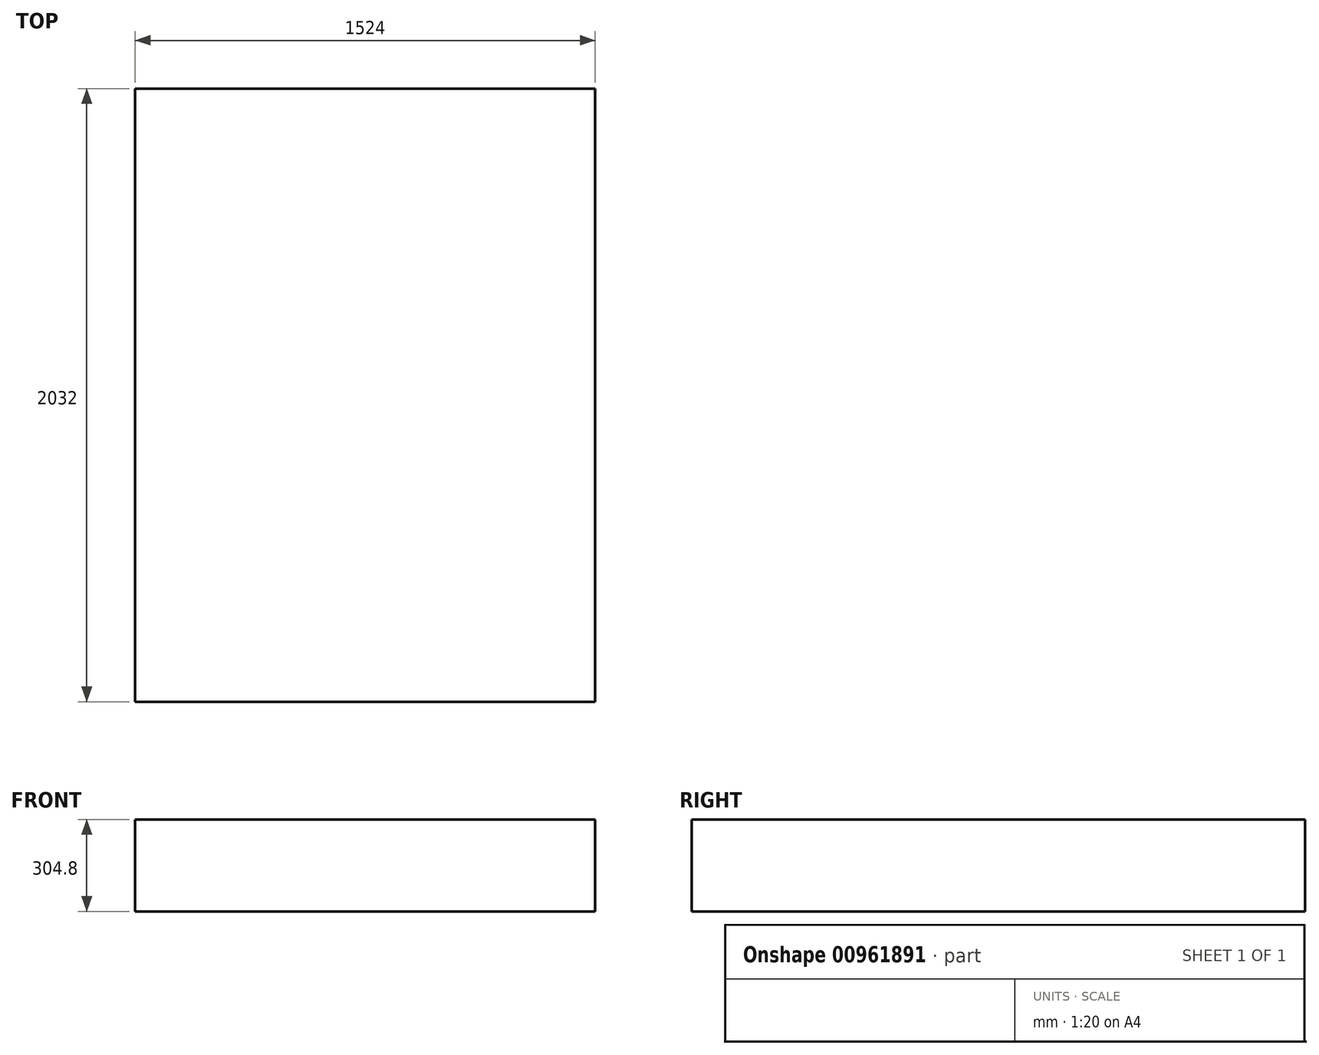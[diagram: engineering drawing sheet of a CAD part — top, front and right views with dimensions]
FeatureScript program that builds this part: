
annotation { "Feature Type Name" : "Feature", "Feature Type Description" : "" }
export const myFeature = defineFeature(function(context is Context, id is Id, definition is map)
    precondition{}
    {
        {
            var Q0;
            Q0=qCreatedBy(makeId("Top.planeOp"),FACE);
            var sketch = newSketch(context, id + "F0", { "sketchPlane" : qUnion([Q0])});
            skLineSegment(sketch, "E0.bottom", {"start": v(-762, 1016) * mm, "end": v(762, 1016) * mm});
            skLineSegment(sketch, "E0.top", {"start": v(-762, -1016) * mm, "end": v(762, -1016) * mm});
            skLineSegment(sketch, "E0.left", {"start": v(-762, 1016) * mm, "end": v(-762, -1016) * mm});
            skLineSegment(sketch, "E0.right", {"start": v(762, 1016) * mm, "end": v(762, -1016) * mm});
            skPoint(sketch, "E0.middle", {"position": v(0, 0) * mm});
            skSolve(sketch);
        }
        {
            var Q0;
            Q0 = qSketchRegion(id + "F0", true);
            extrude(context, id + "F1", {"entities" : qUnion([Q0]), "depth" : 304.8 * mm, "offsetDistance" : 25.4 * mm});
        }
    });
